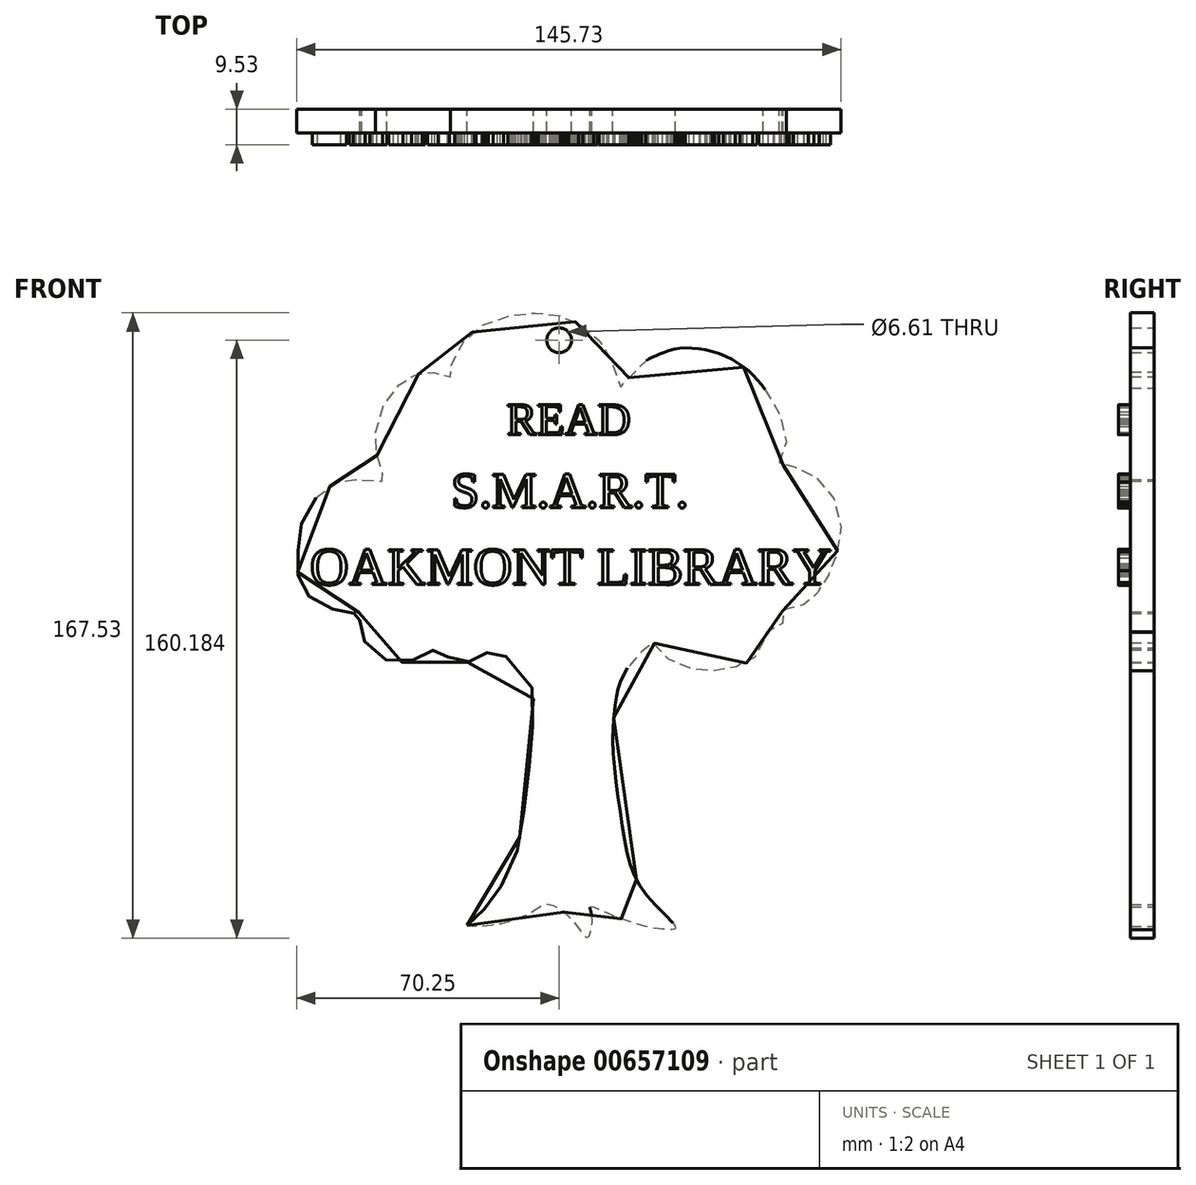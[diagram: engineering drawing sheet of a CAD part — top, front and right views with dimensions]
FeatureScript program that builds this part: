
annotation { "Feature Type Name" : "Feature", "Feature Type Description" : "" }
export const myFeature = defineFeature(function(context is Context, id is Id, definition is map)
    precondition{}
    {
        {
            var Q0;
            Q0=qCreatedBy(makeId("Front.planeOp"),FACE);
            var sketch = newSketch(context, id + "F0", { "sketchPlane" : qUnion([Q0])});
            skText(sketch, "E0", { "text": "OAKMONT LIBRARY\n", "fontName": "Tinos-Regular.ttf"});
            skText(sketch, "E1", { "text": "S.M.A.R.T.", "fontName": "Tinos-Regular.ttf"});
            skText(sketch, "E2", { "text": "READ\n", "fontName": "Tinos-Regular.ttf"});
            const initialGuessF0  = {"E0": [-0.06668, 0.00038, 1, 0, 0.01031], "E1": [-0.0289, 0.02107, 1, 0, 0.00974], "E2": [-0.01407, 0.04057, 1, 0, 0.00878]};
            skSetInitialGuess(sketch, initialGuessF0);
            skSolve(sketch);
        }
        {
            var Q0;
            Q0 = qSketchRegion(id + "F0", true);
            extrude(context, id + "F1", {"entities" : qUnion([Q0]), "depth" : 6.35 * mm, "offsetDistance" : 25.4 * mm});
        }
        {
            var Q0;
            Q0=qCreatedBy(makeId("Front.planeOp"),FACE);
            var sketch = newSketch(context, id + "F2", { "sketchPlane" : qUnion([Q0])});
            skFitSpline(sketch, "E3", {"points": [v(-24.6, -90.92) * mm, v(-22.92, -89.53) * mm, v(-19.73, -86.14) * mm, v(-17.15, -82.76) * mm, v(-12.47, -74.5) * mm, v(-10.28, -66.04) * mm, v(-8.59, -53.6) * mm, v(-7.5, -42.95) * mm, v(-6.9, -33.3) * mm, v(-8.59, -24.04) * mm, v(-16.25, -17.67) * mm, v(-18.34, -17.18) * mm, v(-19.53, -17.97) * mm, v(-21.33, -19.27) * mm, v(-24.11, -20.26) * mm, v(-27.9, -20.16) * mm, v(-29.88, -18.87) * mm, v(-32.37, -16.58) * mm, v(-33.27, -16.78) * mm, v(-35.16, -18.37) * mm, v(-38.64, -19.76) * mm, v(-42.42, -20.46) * mm, v(-47.8, -19.07) * mm, v(-51.68, -15.49) * mm, v(-52.77, -13.1) * mm, v(-53.34, -9.91) * mm, v(-53.06, -7.52) * mm, v(-52.85, -6.96) * mm, v(-54.6, -7.3) * mm, v(-57.07, -7.03) * mm, v(-60.45, -6.18) * mm, v(-65.38, -4.07) * mm, v(-67.63, -1.89) * mm, v(-69.23, 1.22) * mm, v(-70.23, 5.07) * mm, v(-69.9, 9) * mm, v(-69.48, 13.7) * mm, v(-68.56, 17.88) * mm, v(-65.8, 22.9) * mm, v(-59.97, 27.53) * mm, v(-56.8, 28.3) * mm, v(-51.88, 28.45) * mm, v(-46.11, 28.38) * mm, v(-46.53, 29.36) * mm, v(-48.08, 31.9) * mm, v(-48.92, 36.54) * mm, v(-49.14, 40.9) * mm, v(-46.9, 48.6) * mm, v(-42.64, 54.05) * mm, v(-40.04, 55.94) * mm, v(-36.23, 57.1) * mm, v(-33, 57.17) * mm, v(-29.58, 56.22) * mm, v(-28.88, 56.05) * mm, v(-29.02, 57.1) * mm, v(-28.1, 61.4) * mm, v(-23.6, 67.7) * mm, v(-18.37, 70.78) * mm, v(-10.16, 73.02) * mm, v(-3.9, 72.97) * mm, v(1.53, 72.02) * mm, v(6.95, 69.09) * mm, v(11.55, 64.86) * mm, v(14.4, 59.21) * mm, v(16.53, 53.19) * mm, v(16.82, 53.02) * mm, v(17.66, 54.28) * mm, v(22.08, 59.53) * mm, v(25.5, 61.54) * mm, v(32.79, 63.71) * mm, v(46.26, 60.7) * mm, v(55.55, 52.16) * mm, v(59.9, 43.88) * mm, v(60.49, 36.68) * mm, v(58.9, 33) * mm, v(60.15, 32.41) * mm, v(65.76, 31.16) * mm, v(70.87, 26.86) * mm, v(75.1, 19.82) * mm, v(74.67, 9.97) * mm, v(72.98, 5.18) * mm, v(71, 0.81) * mm, v(68.39, -2.7) * mm, v(65.65, -4.96) * mm, v(60.37, -6.22) * mm, v(59.73, -6.79) * mm, v(59.95, -9.04) * mm, v(58.54, -11.36) * mm, v(54.95, -12.34) * mm, v(54.6, -12.34) * mm, v(54.6, -14.88) * mm, v(53.33, -17.9) * mm, v(50.37, -20.5) * mm, v(45.17, -22.13) * mm, v(40.45, -22.69) * mm, v(35.67, -22.27) * mm, v(28.98, -19.31) * mm, v(25.11, -15.16) * mm, v(24.13, -15.93) * mm, v(21.66, -17.9) * mm, v(18.5, -21.56) * mm, v(16.1, -26.35) * mm, v(15.05, -31.34) * mm, v(14.4, -42.2) * mm, v(16.23, -59.65) * mm, v(19.05, -74.56) * mm, v(24.96, -84.56) * mm, v(31.14, -91.6) * mm, v(29.6, -92.01) * mm, v(24.66, -91.45) * mm, v(14.67, -88.35) * mm, v(8.34, -85.96) * mm, v(8.62, -87.8) * mm, v(7.78, -94.27) * mm, v(6.93, -93.84) * mm, v(3, -88.78) * mm, v(-3.34, -85.26) * mm, v(-6.58, -86.95) * mm, v(-11.37, -89.2) * mm, v(-16.3, -90.6) * mm, v(-24.6, -90.92) * mm]});
            skCircle(sketch, "E4", {"center": v(0, 65.83) * mm, "radius": 3.3 * mm});
            skSolve(sketch);
        }
        {
            var Q0;
            Q0 = qSketchRegion(id + "F2", true);
            extrude(context, id + "F3", {"entities" : qUnion([Q0]), "operationType" : NewBodyOperationType.ADD, "endBound" : BoundingType.SYMMETRIC, "depth" : 6.35 * mm, "offsetDistance" : 25.4 * mm});
        }
    });
